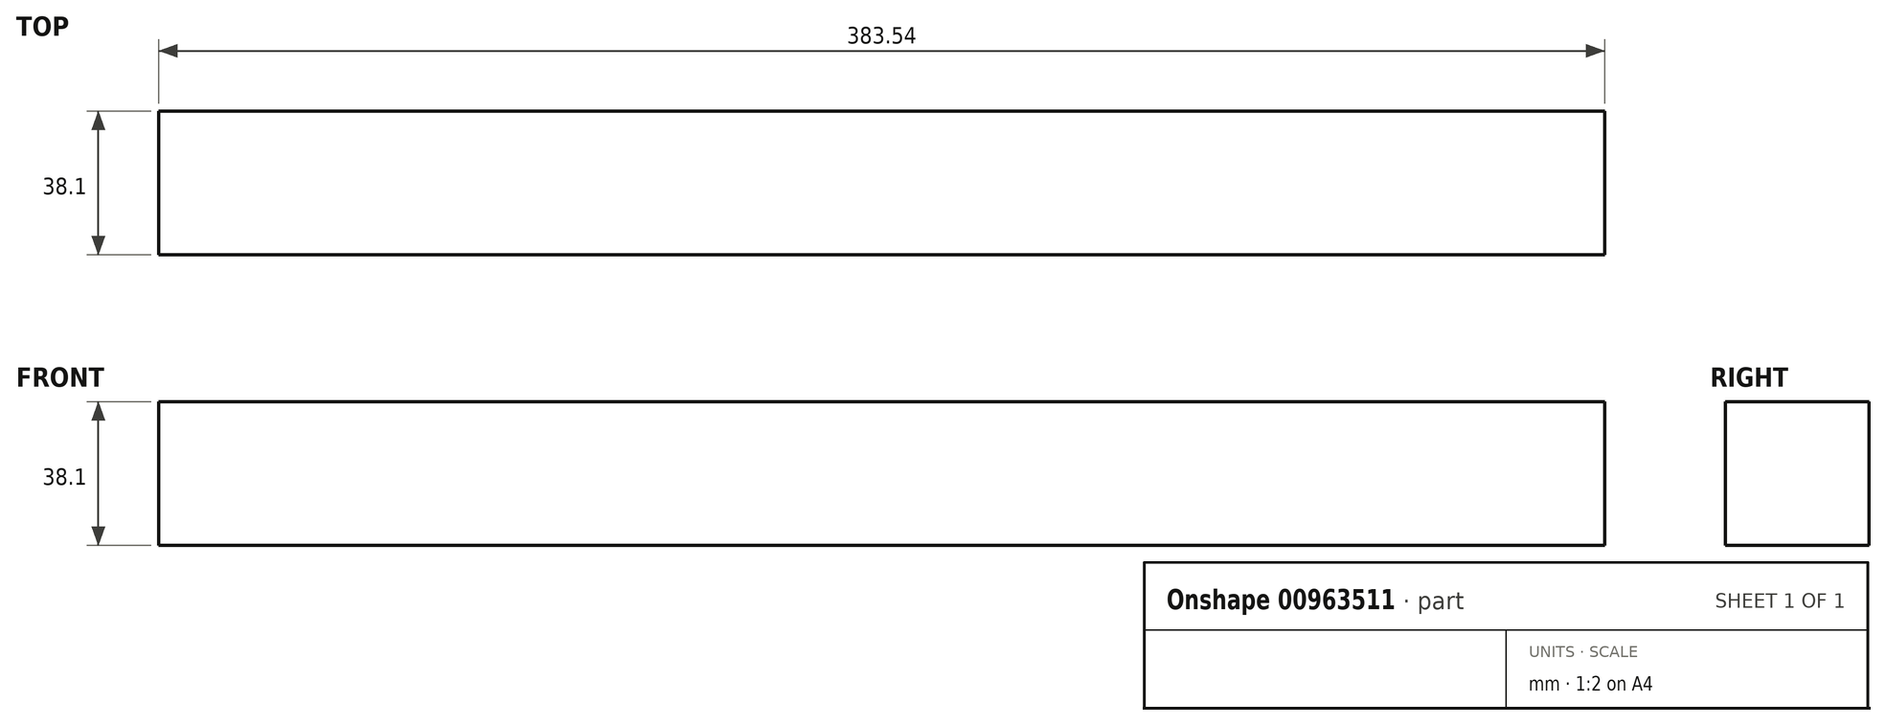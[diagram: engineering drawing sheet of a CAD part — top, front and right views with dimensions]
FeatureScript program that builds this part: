
annotation { "Feature Type Name" : "Feature", "Feature Type Description" : "" }
export const myFeature = defineFeature(function(context is Context, id is Id, definition is map)
    precondition{}
    {
        {
            var Q0;
            Q0=qCreatedBy(makeId("Front.planeOp"),FACE);
            var sketch = newSketch(context, id + "F0", { "sketchPlane" : qUnion([Q0])});
            skLineSegment(sketch, "E0.bottom", {"start": v(191.77, 19.05) * mm, "end": v(-191.77, 19.05) * mm});
            skLineSegment(sketch, "E0.top", {"start": v(191.77, -19.05) * mm, "end": v(-191.77, -19.05) * mm});
            skLineSegment(sketch, "E0.left", {"start": v(191.77, 19.05) * mm, "end": v(191.77, -19.05) * mm});
            skLineSegment(sketch, "E0.right", {"start": v(-191.77, 19.05) * mm, "end": v(-191.77, -19.05) * mm});
            skPoint(sketch, "E0.middle", {"position": v(0, 0) * mm});
            skSolve(sketch);
        }
        {
            var Q0;
            Q0=makeQuery(id+"F0.imprint","IMPRINT",FACE,{"disambiguationData":[TD([[makeQuery(id+"F0.imprint","IMPRINT",EDGE,{"derivedFrom":sQuery(id+"F0.wireOp",EDGE,"E0.bottom")}),1.0]])]});
            extrude(context, id + "F1", {"entities" : qUnion([Q0]), "depth" : 38.1 * mm, "offsetDistance" : 25.4 * mm});
        }
    });
